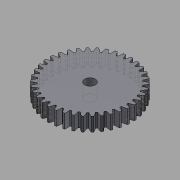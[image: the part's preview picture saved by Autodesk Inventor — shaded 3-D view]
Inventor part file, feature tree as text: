
AUTODESK INVENTOR PART (.ipt)
format: ipt  version: 2015 (Build 190159000, 159)  size: 331,264 bytes
history: native  units: in
note: dims shown in document units (in); Inventor stores cm internally (conversion verified against a paired STEP export)
features: other x13, sketch x3, plane x2
ambient origin geometry x8: Origin, YZ Plane, XZ Plane, XY Plane, X Axis, Y Axis, Z Axis, Center Point
bodies: Solid1 (feature_tree)
feature tree (18):
  other  "Spur Gear2"
  other  "Solid1::Spur Gear2"
  other  "TaggingFeature1"
  sketch  "Sketch1"  dims[d0=0.3937in]
  sketch  "Sketch2"  dims[d16=0.4724in d17=0.0in d41=0.0in d43=0.4724in d46=0.4724in d47=0.0in d48=0.0in]
  sketch  "Sketch3"
  plane  "XZ Plane_1"
  plane  "Work Plane2"
  other  "Z Axis_1"
  other  "Srf1"
  other  "Srf1::Derived"
  other  "Distance iMate"
  other  "Align iMate"
  other  "Mesh iMate"
  other  "Axis iMate"
  other  "Position iMate"
  other  "Mesh iMate2"
  other  "Start plane iMate"
